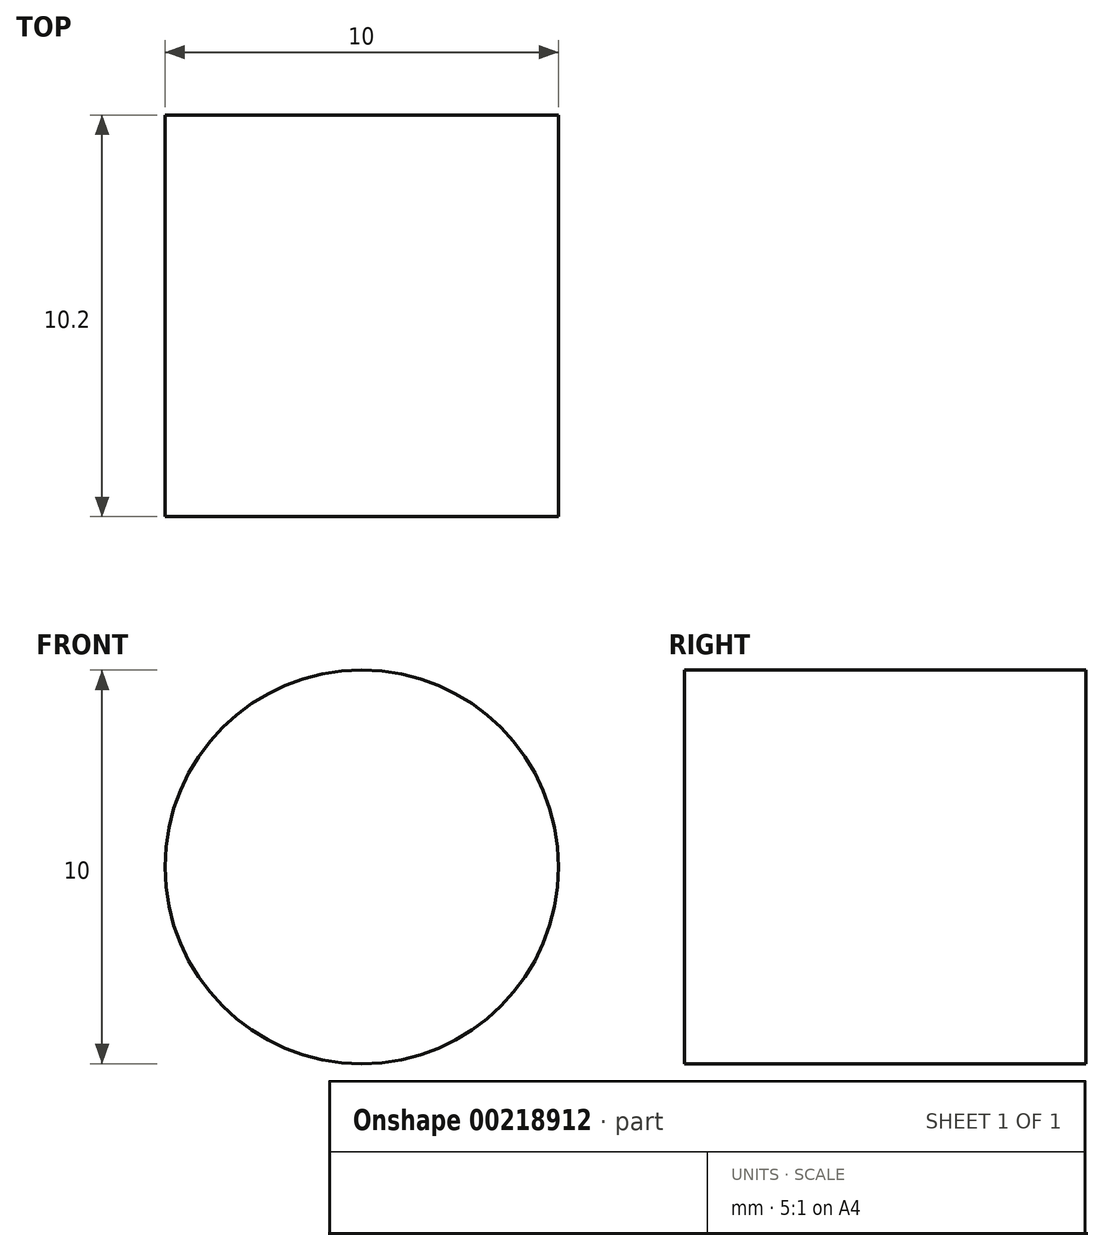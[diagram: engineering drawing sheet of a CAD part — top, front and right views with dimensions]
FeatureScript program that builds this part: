
annotation { "Feature Type Name" : "Feature", "Feature Type Description" : "" }
export const myFeature = defineFeature(function(context is Context, id is Id, definition is map)
    precondition{}
    {
        {
            var Q0;
            Q0=qCreatedBy(makeId("Front.planeOp"),FACE);
            var sketch = newSketch(context, id + "F0", { "sketchPlane" : qUnion([Q0])});
            skCircle(sketch, "E0", {"center": v(0, 0) * mm, "radius": 5 * mm});
            skSolve(sketch);
        }
        {
            var Q0;
            Q0 = qSketchRegion(id + "F0", true);
            extrude(context, id + "F1", {"entities" : qUnion([Q0]), "depth" : 10.2 * mm});
        }
    });
